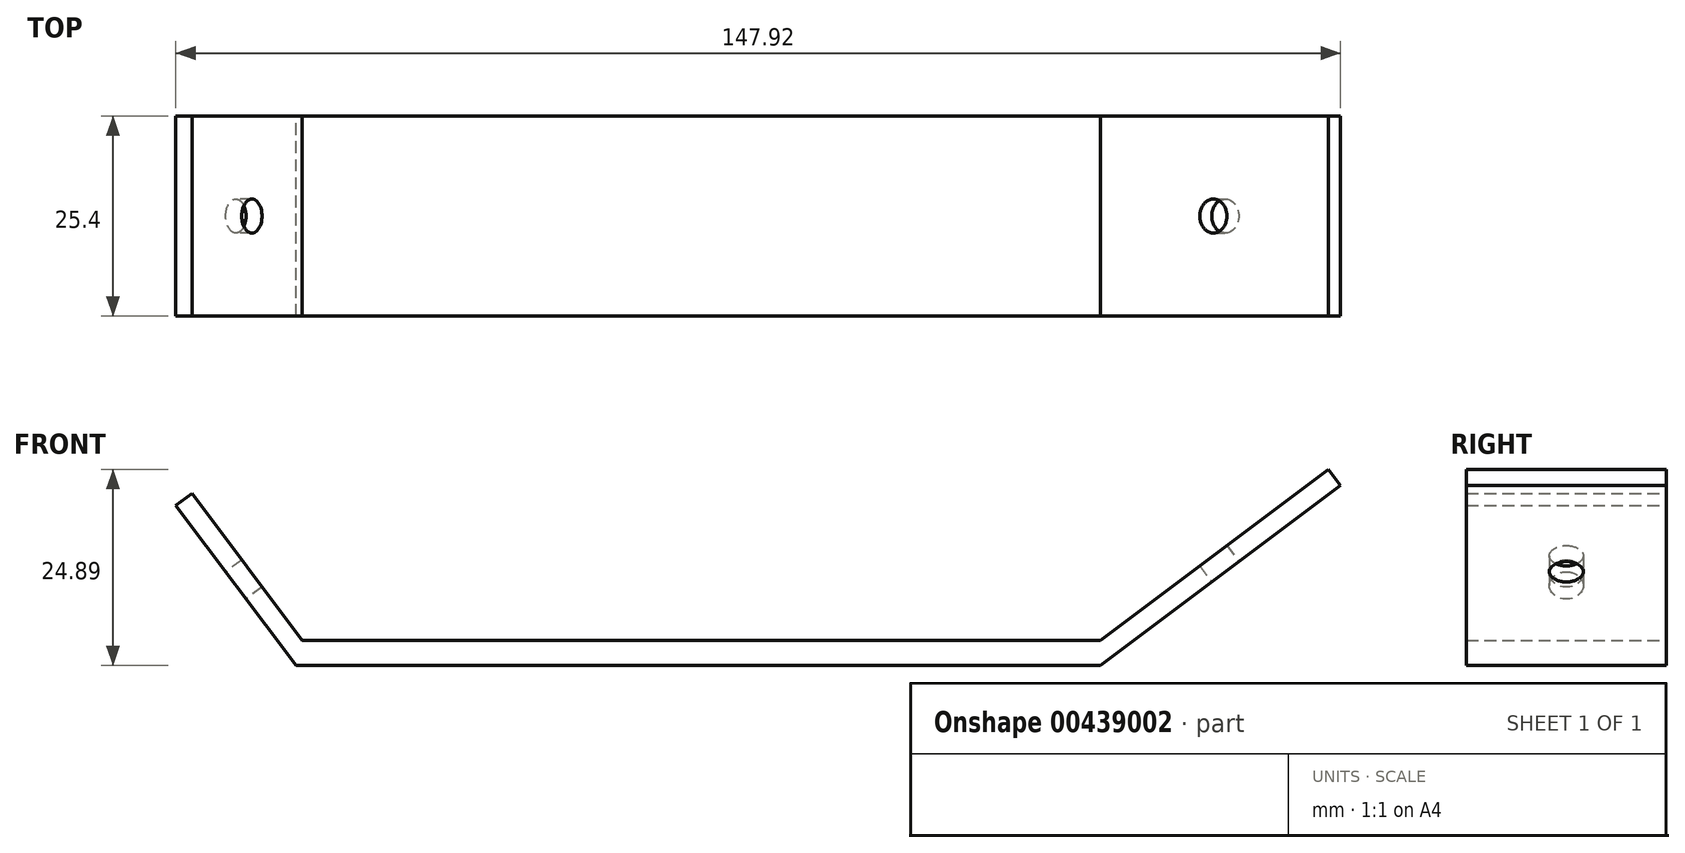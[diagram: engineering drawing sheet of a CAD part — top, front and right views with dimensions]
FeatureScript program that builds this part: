
annotation { "Feature Type Name" : "Feature", "Feature Type Description" : "" }
export const myFeature = defineFeature(function(context is Context, id is Id, definition is map)
    precondition{}
    {
        {
            var Q0;
            Q0=qCreatedBy(makeId("Front.planeOp"),FACE);
            var sketch = newSketch(context, id + "F0", { "sketchPlane" : qUnion([Q0])});
            skPoint(sketch, "E0.0.midPoint", {"position": v(-22.86, 0) * mm});
            skLineSegment(sketch, "E1", {"start": v(0, -30.48) * mm, "end": v(0, 30.48) * mm, "construction": true});
            skLineSegment(sketch, "E2.bottom", {"start": v(35.52, 16.45) * mm, "end": v(-66.68, 16.45) * mm});
            skLineSegment(sketch, "E2.top", {"start": v(35.52, 19.63) * mm, "end": v(-65.89, 19.63) * mm});
            skLineSegment(sketch, "E3", {"start": v(35.52, 16.45) * mm, "end": v(66, 39.31) * mm});
            skLineSegment(sketch, "E4", {"start": v(35.52, 19.63) * mm, "end": v(64.47, 41.34) * mm});
            skLineSegment(sketch, "E5", {"start": v(66, 39.31) * mm, "end": v(64.47, 41.34) * mm});
            skLineSegment(sketch, "E6", {"start": v(-66.68, 16.45) * mm, "end": v(-81.92, 36.77) * mm});
            skLineSegment(sketch, "E7", {"start": v(-65.89, 19.63) * mm, "end": v(-79.89, 38.3) * mm});
            skLineSegment(sketch, "E8", {"start": v(-81.92, 36.77) * mm, "end": v(-79.89, 38.3) * mm});
            skPoint(sketch, "E9", {"position": v(-72.89, 28.96) * mm});
            skPoint(sketch, "E10", {"position": v(50, 30.48) * mm});
            skPoint(sketch, "E11", {"position": v(-74.3, 26.61) * mm});
            skPoint(sketch, "E12", {"position": v(50.76, 27.88) * mm});
            skSolve(sketch);
        }
        {
            var Q0;
            Q0=makeQuery(id+"F0.imprint","IMPRINT",FACE,{"disambiguationData":[TD([[makeQuery(id+"F0.imprint","IMPRINT",EDGE,{"derivedFrom":sQuery(id+"F0.wireOp",EDGE,"E2.bottom")}),-1.0]])]});
            extrude(context, id + "F1", {"entities" : qUnion([Q0]), "depth" : 25.4 * mm, "offsetDistance" : 25.4 * mm});
        }
        {
            var Q0;
            Q0=makeQuery(id+"F1.opExtrude","SWEPT_FACE",FACE,{"disambiguationData":[OSD([sQuery(id+"F0.wireOp",EDGE,"E3")])]});
            var sketch = newSketch(context, id + "F2", { "sketchPlane" : qUnion([Q0])});
            skLineSegment(sketch, "E13", {"start": v(76.38, 12.7) * mm, "end": v(38.28, 12.7) * mm, "construction": true});
            skLineSegment(sketch, "E14", {"start": v(57.33, 25.4) * mm, "end": v(57.33, 0) * mm, "construction": true});
            skCircle(sketch, "E15", {"center": v(58.12, 12.7) * mm, "radius": 2.15 * mm});
            skSolve(sketch);
        }
        {
            var Q0;
            Q0=makeQuery(id+"F1.opExtrude","SWEPT_FACE",FACE,{"disambiguationData":[OSD([sQuery(id+"F0.wireOp",EDGE,"E6")])]});
            var sketch = newSketch(context, id + "F3", { "sketchPlane" : qUnion([Q0])});
            skLineSegment(sketch, "E16", {"start": v(12.7, 78.57) * mm, "end": v(12.7, 53.17) * mm, "construction": true});
            skLineSegment(sketch, "E17", {"start": v(0, 65.87) * mm, "end": v(25.4, 65.87) * mm, "construction": true});
            skCircle(sketch, "E18", {"center": v(12.7, 65.87) * mm, "radius": 2.15 * mm});
            skSolve(sketch);
        }
        {
            var Q0;
            Q0=makeQuery(id+"F2.imprint","IMPRINT",FACE,{"disambiguationData":[TD([[makeQuery(id+"F2.imprint","IMPRINT",EDGE,{"derivedFrom":sQuery(id+"F2.wireOp",EDGE,"E15")}),1.0]])]});
            extrude(context, id + "F4", {"entities" : qUnion([Q0]), "operationType" : NewBodyOperationType.REMOVE, "oppositeDirection" : true, "depth" : 25.4 * mm, "offsetDistance" : 25.4 * mm});
        }
        {
            var Q0;
            Q0=makeQuery(id+"F3.imprint","IMPRINT",FACE,{"disambiguationData":[TD([[makeQuery(id+"F3.imprint","IMPRINT",EDGE,{"derivedFrom":sQuery(id+"F3.wireOp",EDGE,"E18")}),1.0]])]});
            extrude(context, id + "F5", {"entities" : qUnion([Q0]), "operationType" : NewBodyOperationType.REMOVE, "oppositeDirection" : true, "depth" : 25.4 * mm, "offsetDistance" : 25.4 * mm});
        }
    });
